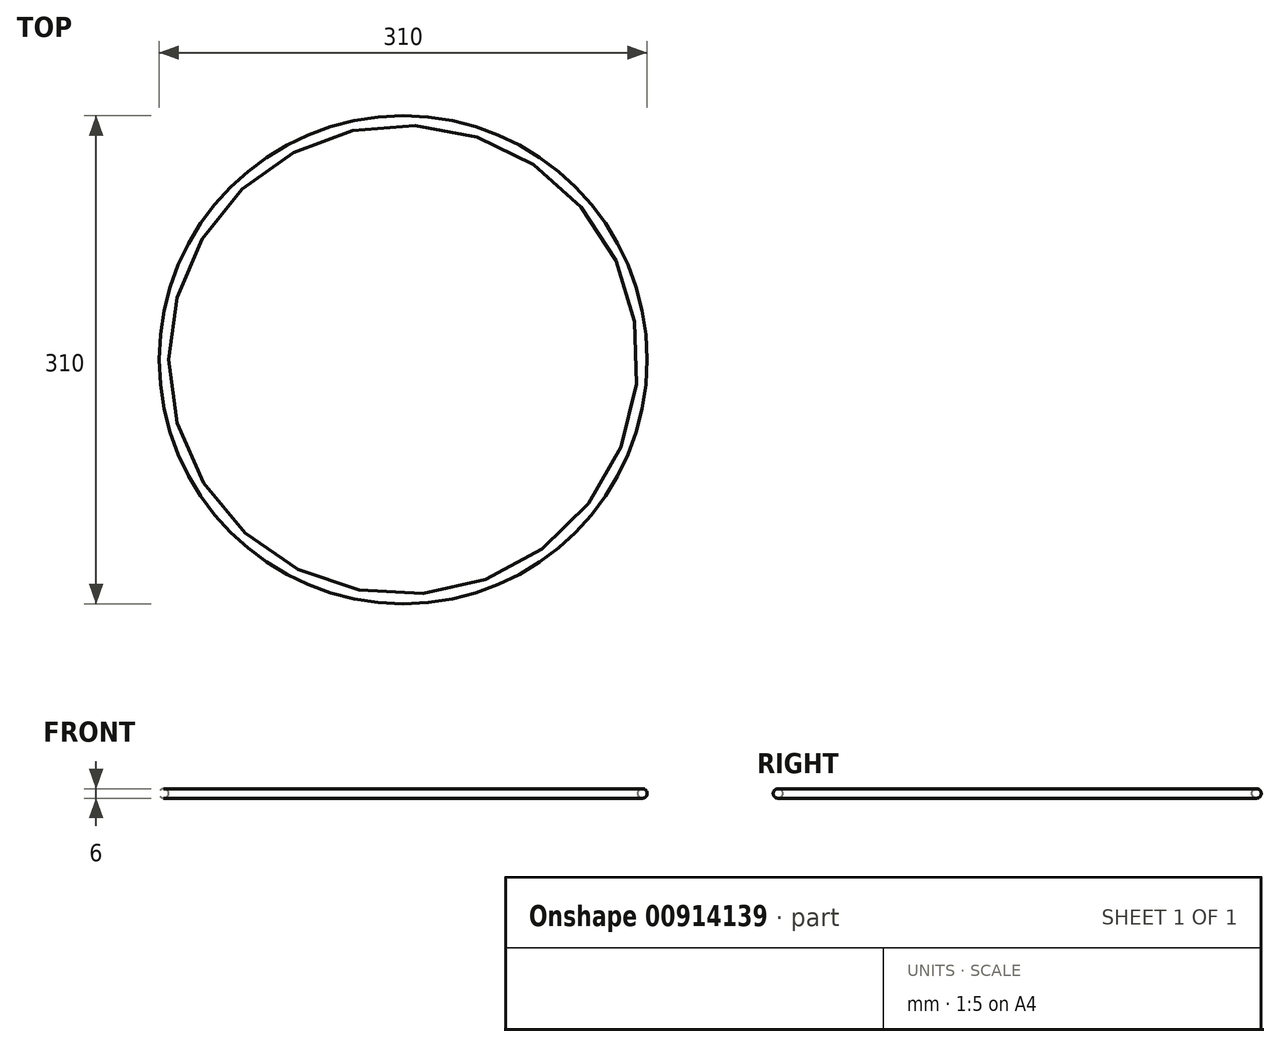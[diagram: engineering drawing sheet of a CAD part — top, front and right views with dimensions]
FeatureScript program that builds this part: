
annotation { "Feature Type Name" : "Feature", "Feature Type Description" : "" }
export const myFeature = defineFeature(function(context is Context, id is Id, definition is map)
    precondition{}
    {
        {
            var Q0;
            Q0=qCreatedBy(makeId("Right.planeOp"),FACE);
            var sketch = newSketch(context, id + "F0", { "sketchPlane" : qUnion([Q0])});
            skCircle(sketch, "E0", {"center": v(152, 0) * mm, "radius": 3 * mm});
            skSolve(sketch);
        }
        {
            var Q0;
            Q0=qCreatedBy(makeId("Front.planeOp"),FACE);
            var sketch = newSketch(context, id + "F1", { "sketchPlane" : qUnion([Q0])});
            skLineSegment(sketch, "E1", {"start": v(0, 0) * mm, "end": v(0, 44.03) * mm, "construction": true});
            skSolve(sketch);
        }
        {
            var Q0;
            Q0=makeQuery(id+"F0.imprint","IMPRINT",FACE,{"disambiguationData":[TD([[makeQuery(id+"F0.imprint","IMPRINT",EDGE,{"derivedFrom":sQuery(id+"F0.wireOp",EDGE,"E0")}),1.0]])]});
            var Q1;
            Q1=sQuery(id+"F1.wireOp",EDGE,"E1");
            revolve(context, id + "F2", {"surfaceOperationType" : NewSurfaceOperationType.NEW, "entities" : qUnion([Q0]), "axis" : qUnion([Q1]), "revolveType" : RevolveType.FULL});
        }
    });
